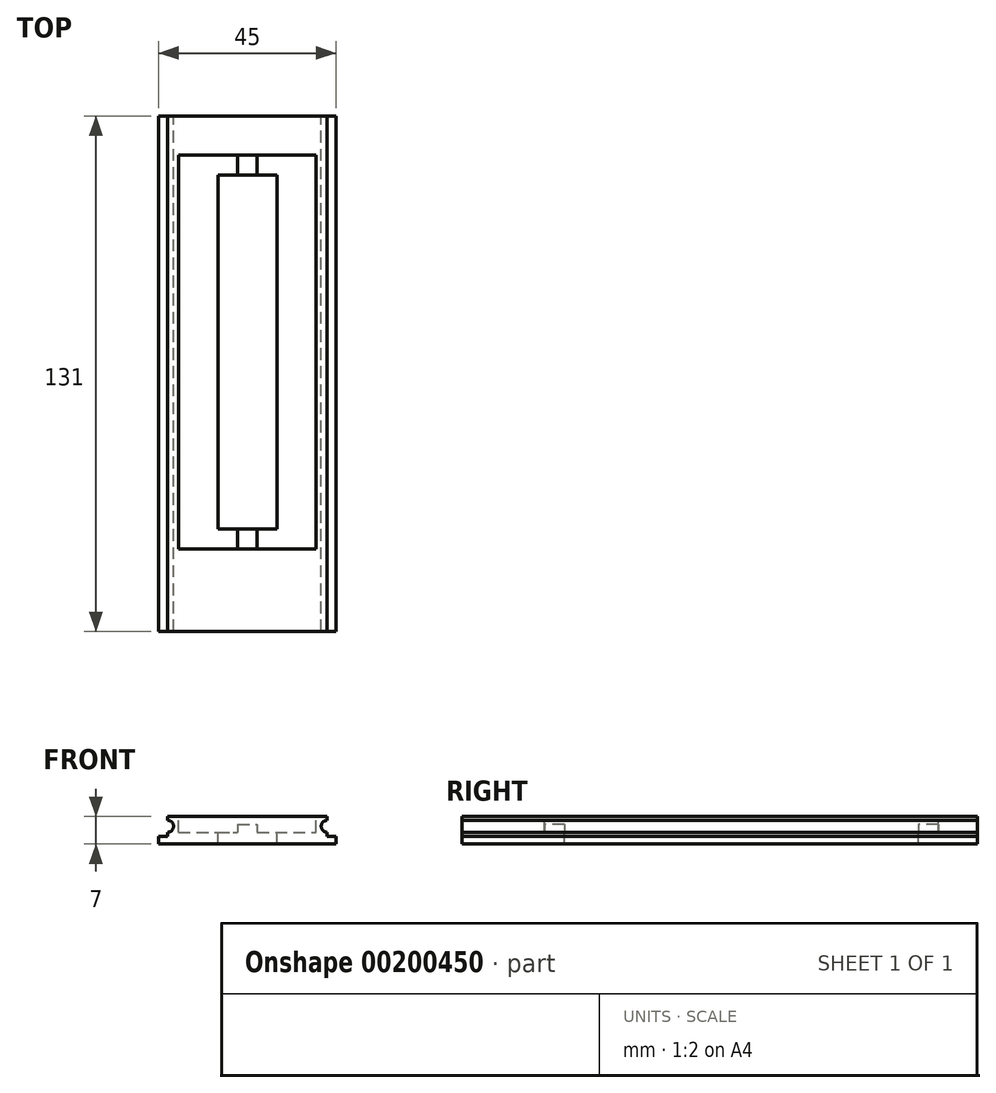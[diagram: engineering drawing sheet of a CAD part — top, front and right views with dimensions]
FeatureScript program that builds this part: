
annotation { "Feature Type Name" : "Feature", "Feature Type Description" : "" }
export const myFeature = defineFeature(function(context is Context, id is Id, definition is map)
    precondition{}
    {
        {
            var Q0;
            Q0=qCreatedBy(makeId("Top.planeOp"),FACE);
            var sketch = newSketch(context, id + "F0", { "sketchPlane" : qUnion([Q0])});
            skLineSegment(sketch, "E0.bottom", {"start": v(0, 0) * mm, "end": v(45, 0) * mm});
            skLineSegment(sketch, "E0.top", {"start": v(0, 131) * mm, "end": v(45, 131) * mm});
            skLineSegment(sketch, "E0.left", {"start": v(0, 0) * mm, "end": v(0, 131) * mm});
            skLineSegment(sketch, "E0.right", {"start": v(45, 0) * mm, "end": v(45, 131) * mm});
            skSolve(sketch);
        }
        {
            var Q0;
            Q0 = qSketchRegion(id + "F0", true);
            extrude(context, id + "F1", {"entities" : qUnion([Q0]), "depth" : 2 * mm});
        }
        {
            var Q0;
            Q0=makeQuery(id+"F1.opExtrude","CAP_FACE",FACE,{"disambiguationData":[OSD([sQuery(id+"F0.wireOp",EDGE,"E0.bottom"),sQuery(id+"F0.wireOp",EDGE,"E0.top"),sQuery(id+"F0.wireOp",EDGE,"E0.left"),sQuery(id+"F0.wireOp",EDGE,"E0.right")])],"isStart":false});
            var sketch = newSketch(context, id + "F2", { "sketchPlane" : qUnion([Q0])});
            skLineSegment(sketch, "E1.bottom", {"start": v(2.25, 0) * mm, "end": v(42.75, 0) * mm});
            skLineSegment(sketch, "E1.top", {"start": v(2.25, 131) * mm, "end": v(42.75, 131) * mm});
            skLineSegment(sketch, "E1.left", {"start": v(2.25, 0) * mm, "end": v(2.25, 131) * mm});
            skLineSegment(sketch, "E1.right", {"start": v(42.75, 0) * mm, "end": v(42.75, 131) * mm});
            skSolve(sketch);
        }
        {
            var Q0;
            Q0 = qSketchRegion(id + "F2", true);
            extrude(context, id + "F3", {"entities" : qUnion([Q0]), "operationType" : NewBodyOperationType.ADD, "depth" : 5 * mm});
        }
        {
            var Q0;
            Q0=makeQuery(id+"F3.opExtrude","CAP_FACE",FACE,{"disambiguationData":[OSD([sQuery(id+"F2.wireOp",EDGE,"E1.bottom"),sQuery(id+"F2.wireOp",EDGE,"E1.top"),sQuery(id+"F2.wireOp",EDGE,"E1.left"),sQuery(id+"F2.wireOp",EDGE,"E1.right")])],"isStart":false});
            var sketch = newSketch(context, id + "F4", { "sketchPlane" : qUnion([Q0])});
            skLineSegment(sketch, "E2.bottom", {"start": v(15, 116) * mm, "end": v(30, 116) * mm});
            skLineSegment(sketch, "E2.top", {"start": v(15, 26) * mm, "end": v(30, 26) * mm});
            skLineSegment(sketch, "E2.left", {"start": v(15, 116) * mm, "end": v(15, 26) * mm});
            skLineSegment(sketch, "E2.right", {"start": v(30, 116) * mm, "end": v(30, 26) * mm});
            skSolve(sketch);
        }
        {
            var Q0;
            Q0=makeQuery(id+"F3.opExtrude","CAP_FACE",FACE,{"disambiguationData":[OSD([sQuery(id+"F2.wireOp",EDGE,"E1.bottom"),sQuery(id+"F2.wireOp",EDGE,"E1.top"),sQuery(id+"F2.wireOp",EDGE,"E1.left"),sQuery(id+"F2.wireOp",EDGE,"E1.right")])],"isStart":false});
            var sketch = newSketch(context, id + "F5", { "sketchPlane" : qUnion([Q0])});
            skLineSegment(sketch, "E3.bottom", {"start": v(5, 121) * mm, "end": v(40, 121) * mm});
            skLineSegment(sketch, "E3.top", {"start": v(5, 21) * mm, "end": v(40, 21) * mm});
            skLineSegment(sketch, "E3.left", {"start": v(5, 121) * mm, "end": v(5, 21) * mm});
            skLineSegment(sketch, "E3.right", {"start": v(40, 121) * mm, "end": v(40, 21) * mm});
            skSolve(sketch);
        }
        {
            var Q0;
            Q0 = qSketchRegion(id + "F5", true);
            extrude(context, id + "F6", {"entities" : qUnion([Q0]), "operationType" : NewBodyOperationType.REMOVE, "oppositeDirection" : true, "depth" : 4 * mm});
        }
        {
            var Q0;
            Q0=makeQuery(id+"F6.boolean.opBoolean","COPY",FACE,{"derivedFrom":makeQuery(id+"F6.opExtrude","CAP_FACE",FACE,{"disambiguationData":[OSD([sQuery(id+"F5.wireOp",EDGE,"E3.bottom"),sQuery(id+"F5.wireOp",EDGE,"E3.top"),sQuery(id+"F5.wireOp",EDGE,"E3.left"),sQuery(id+"F5.wireOp",EDGE,"E3.right")])],"isStart":false})});
            var sketch = newSketch(context, id + "F7", { "sketchPlane" : qUnion([Q0])});
            skLineSegment(sketch, "E4.bottom", {"start": v(20, 121) * mm, "end": v(25, 121) * mm});
            skLineSegment(sketch, "E4.top", {"start": v(20, 21) * mm, "end": v(25, 21) * mm});
            skLineSegment(sketch, "E4.left", {"start": v(20, 121) * mm, "end": v(20, 21) * mm});
            skLineSegment(sketch, "E4.right", {"start": v(25, 121) * mm, "end": v(25, 21) * mm});
            skSolve(sketch);
        }
        {
            var Q0;
            Q0 = qSketchRegion(id + "F7", true);
            extrude(context, id + "F8", {"entities" : qUnion([Q0]), "operationType" : NewBodyOperationType.ADD, "depth" : 2 * mm});
        }
        {
            var Q0;
            Q0 = qSketchRegion(id + "F4", true);
            extrude(context, id + "F9", {"entities" : qUnion([Q0]), "operationType" : NewBodyOperationType.REMOVE, "endBound" : BoundingType.THROUGH_ALL, "oppositeDirection" : true, "depth" : 25.4 * mm});
        }
        {
            var Q0;
            Q0=makeQuery(id+"F3.boolean.opBoolean","MERGE",FACE,{"derivedFrom":[makeQuery(id+"F1.opExtrude","SWEPT_FACE",FACE,{"disambiguationData":[OSD([sQuery(id+"F0.wireOp",EDGE,"E0.top")])]}),makeQuery(id+"F3.opExtrude","SWEPT_FACE",FACE,{"disambiguationData":[OSD([sQuery(id+"F2.wireOp",EDGE,"E1.top")])]})]});
            var sketch = newSketch(context, id + "F10", { "sketchPlane" : qUnion([Q0])});
            skCircle(sketch, "E5", {"center": v(-42.75, 4.5) * mm, "radius": 1.5 * mm});
            skCircle(sketch, "E6", {"center": v(-2.25, 4.5) * mm, "radius": 1.5 * mm});
            skSolve(sketch);
        }
        {
            var Q0;
            Q0 = qSketchRegion(id + "F10", true);
            extrude(context, id + "F11", {"entities" : qUnion([Q0]), "operationType" : NewBodyOperationType.REMOVE, "endBound" : BoundingType.THROUGH_ALL, "oppositeDirection" : true, "depth" : 25.4 * mm});
        }
    });
